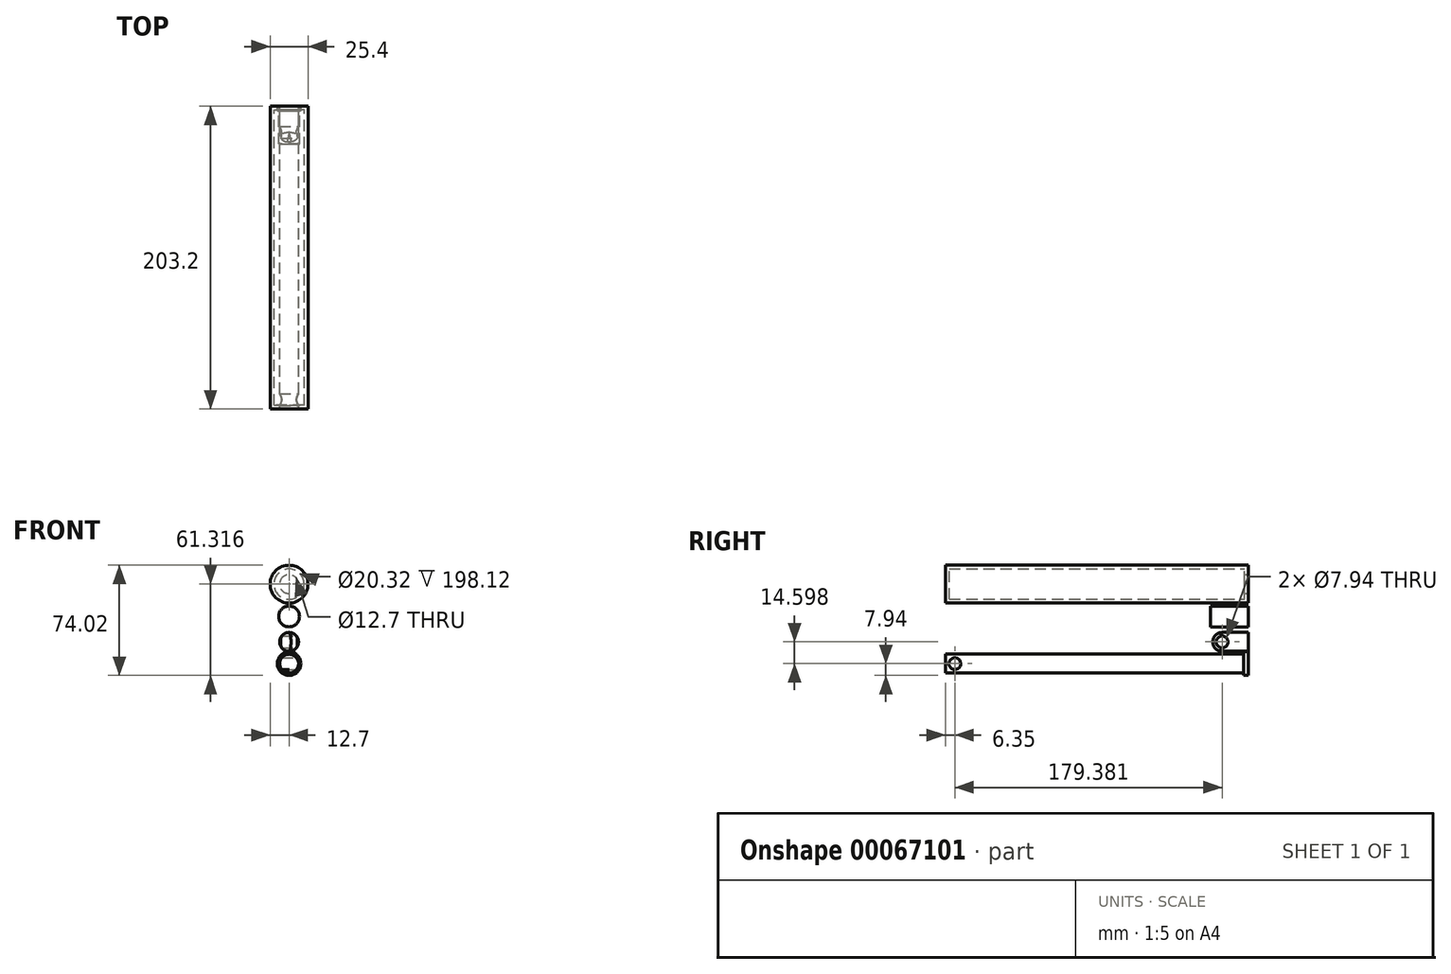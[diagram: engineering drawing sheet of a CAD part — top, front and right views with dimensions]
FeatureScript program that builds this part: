
annotation { "Feature Type Name" : "Feature", "Feature Type Description" : "" }
export const myFeature = defineFeature(function(context is Context, id is Id, definition is map)
    precondition{}
    {
        {
            var Q0;
            Q0=qCreatedBy(makeId("Front.planeOp"),FACE);
            var sketch = newSketch(context, id + "F0", { "sketchPlane" : qUnion([Q0])});
            skCircle(sketch, "E0", {"center": v(0, 0) * mm, "radius": 6.35 * mm});
            skCircle(sketch, "E1", {"center": v(0, 53.38) * mm, "radius": 12.7 * mm});
            skCircle(sketch, "E2", {"center": v(0, 31.7) * mm, "radius": 6.99 * mm});
            skCircle(sketch, "E3", {"center": v(0, 14.6) * mm, "radius": 6.35 * mm});
            skSolve(sketch);
        }
        {
            var Q0;
            Q0=makeQuery(id+"F0.imprint","IMPRINT",FACE,{"disambiguationData":[TD([[makeQuery(id+"F0.imprint","IMPRINT",EDGE,{"derivedFrom":sQuery(id+"F0.wireOp",EDGE,"E1")}),1.0]])]});
            var Q1;
            Q1=makeQuery(id+"F0.imprint","IMPRINT",FACE,{"disambiguationData":[TD([[makeQuery(id+"F0.imprint","IMPRINT",EDGE,{"derivedFrom":sQuery(id+"F0.wireOp",EDGE,"E0")}),1.0]])]});
            extrude(context, id + "F1", {"entities" : qUnion([Q0, Q1]), "depth" : 203.2 * mm});
        }
        {
            var Q0;
            Q0=makeQuery(id+"F0.imprint","IMPRINT",FACE,{"disambiguationData":[TD([[makeQuery(id+"F0.imprint","IMPRINT",EDGE,{"derivedFrom":sQuery(id+"F0.wireOp",EDGE,"E2")}),1.0]])]});
            var Q1;
            Q1=makeQuery(id+"F0.imprint","IMPRINT",FACE,{"disambiguationData":[TD([[makeQuery(id+"F0.imprint","IMPRINT",EDGE,{"derivedFrom":sQuery(id+"F0.wireOp",EDGE,"E3")}),1.0]])]});
            extrude(context, id + "F2", {"entities" : qUnion([Q0, Q1]), "depth" : 25.4 * mm});
        }
        {
            var Q0;
            Q0=makeQuery(id+"F1.opExtrude","CAP_FACE",FACE,{"disambiguationData":[OSD([sQuery(id+"F0.wireOp",EDGE,"E1")])],"isStart":false});
            var Q1;
            Q1=makeQuery(id+"F1.opExtrude","SWEPT_BODY",BODY,{"disambiguationData":[OSD([sQuery(id+"F0.wireOp",EDGE,"E1")])]});
            shell(context, id + "F3", {"isHollow" : true, "entities" : qUnion([Q0]), "parts" : qUnion([Q1]), "thickness" : 2.54 * mm});
        }
        {
            var Q0;
            Q0=makeQuery(id+"F0.imprint","IMPRINT",FACE,{"disambiguationData":[TD([[makeQuery(id+"F0.imprint","IMPRINT",EDGE,{"derivedFrom":sQuery(id+"F0.wireOp",EDGE,"E0")}),1.0]])]});
            var sketch = newSketch(context, id + "F4", { "sketchPlane" : qUnion([Q0])});
            skCircle(sketch, "E4.0", {"center": v(0, 0) * mm, "radius": 6.35 * mm});
            skCircle(sketch, "E4.1", {"center": v(0, 53.38) * mm, "radius": 12.7 * mm});
            skCircle(sketch, "E5", {"center": v(0, 53.38) * mm, "radius": 6.35 * mm});
            skCircle(sketch, "E6", {"center": v(0, 0) * mm, "radius": 7.94 * mm});
            skSolve(sketch);
        }
        {
            var Q0;
            Q0=makeQuery(id+"F4.imprint","IMPRINT",FACE,{"disambiguationData":[TD([[makeQuery(id+"F4.imprint","IMPRINT",EDGE,{"derivedFrom":sQuery(id+"F4.wireOp",EDGE,"E5")}),1.0]])]});
            extrude(context, id + "F5", {"entities" : qUnion([Q0]), "operationType" : NewBodyOperationType.REMOVE, "depth" : 200.66 * mm});
        }
        {
            var Q0;
            Q0=makeQuery(id+"F4.imprint","IMPRINT",FACE,{"disambiguationData":[TD([[makeQuery(id+"F4.imprint","IMPRINT",EDGE,{"derivedFrom":sQuery(id+"F4.wireOp",EDGE,"E4.0")}),-1.0]])]});
            extrude(context, id + "F6", {"entities" : qUnion([Q0]), "operationType" : NewBodyOperationType.ADD, "depth" : 3.17 * mm});
        }
        {
            var Q0;
            Q0=qCreatedBy(makeId("Right.planeOp"),FACE);
            var sketch = newSketch(context, id + "F7", { "sketchPlane" : qUnion([Q0])});
            skLineSegment(sketch, "E7.0", {"start": v(-203.2, -6.35) * mm, "end": v(-203.2, 6.35) * mm});
            skLineSegment(sketch, "E8", {"start": v(-203.2, 6.35) * mm, "end": v(-196.85, 0) * mm});
            skLineSegment(sketch, "E9", {"start": v(-196.85, 0) * mm, "end": v(-203.2, -6.35) * mm});
            skCircle(sketch, "E10", {"center": v(-196.85, 0) * mm, "radius": 3.97 * mm});
            skSolve(sketch);
        }
        {
            var Q0;
            Q0=qCreatedBy(makeId("Right.planeOp"),FACE);
            cPlane(context, id + "F8", {"entities" : qUnion([Q0]), "cplaneType" : CPlaneType.OFFSET, "offset" : 50.8 * mm, "width" : 152.4 * mm, "height" : 152.4 * mm});
        }
        {
            var Q0;
            Q0=qCreatedBy(id+"F8.planeOp",FACE);
            var sketch = newSketch(context, id + "F9", { "sketchPlane" : qUnion([Q0])});
            skCircle(sketch, "E11.0", {"center": v(-196.85, 0) * mm, "radius": 3.97 * mm});
            skSolve(sketch);
        }
        {
            var Q0;
            Q0=makeQuery(id+"F9.imprint","IMPRINT",FACE,{"disambiguationData":[TD([[makeQuery(id+"F9.imprint","IMPRINT",EDGE,{"derivedFrom":sQuery(id+"F9.wireOp",EDGE,"E11.0")}),1.0]])]});
            extrude(context, id + "F10", {"entities" : qUnion([Q0]), "operationType" : NewBodyOperationType.REMOVE, "endBound" : BoundingType.THROUGH_ALL, "oppositeDirection" : true, "depth" : 25.4 * mm});
        }
        {
            var Q0;
            Q0=qCreatedBy(id+"F8.planeOp",FACE);
            var sketch = newSketch(context, id + "F11", { "sketchPlane" : qUnion([Q0])});
            skLineSegment(sketch, "E12.0", {"start": v(-25.4, 8.25) * mm, "end": v(-25.4, 20.95) * mm});
            skLineSegment(sketch, "E13", {"start": v(-25.4, 20.95) * mm, "end": v(-17.47, 14.6) * mm, "construction": true});
            skLineSegment(sketch, "E14", {"start": v(-17.47, 14.6) * mm, "end": v(-25.4, 8.25) * mm, "construction": true});
            skLineSegment(sketch, "E15", {"start": v(-25.4, 14.6) * mm, "end": v(-7.03, 14.6) * mm, "construction": true});
            skCircle(sketch, "E16", {"center": v(-17.47, 14.6) * mm, "radius": 3.97 * mm});
            skCircle(sketch, "E17", {"center": v(-17.47, 14.6) * mm, "radius": 6.35 * mm});
            skLineSegment(sketch, "E18.0", {"start": v(0, 8.25) * mm, "end": v(0, 20.95) * mm});
            skLineSegment(sketch, "E19", {"start": v(-25.4, 20.95) * mm, "end": v(0, 20.95) * mm});
            skLineSegment(sketch, "E20", {"start": v(0, 8.25) * mm, "end": v(-25.4, 8.25) * mm});
            skSolve(sketch);
        }
        {
            var Q0;
            Q0=makeQuery(id+"F11.imprint","IMPRINT",FACE,{"disambiguationData":[TD([[makeQuery(id+"F11.imprint","IMPRINT",EDGE,{"derivedFrom":sQuery(id+"F11.wireOp",EDGE,"E16")}),1.0]])]});
            var Q1;
            {var subQ0=sQuery(id+"F11.wireOp",EDGE,"E12.0");Q1=makeQuery(id+"F11.imprint","IMPRINT",FACE,{"disambiguationData":[TD([[makeQuery(id+"F11.imprint","IMPRINT",EDGE,{"derivedFrom":subQ0}),-1.0]])]});}
            extrude(context, id + "F12", {"entities" : qUnion([Q0, Q1]), "operationType" : NewBodyOperationType.REMOVE, "endBound" : BoundingType.THROUGH_ALL, "oppositeDirection" : true, "depth" : 25.4 * mm});
        }
        {
            var Q0;
            Q0=makeQuery(id+"F12.boolean.opBoolean","INTERSECT",EDGE,{"disambiguationData":[OD(1.0)],"derivedFrom":[makeQuery(id+"F2.opExtrude","SWEPT_FACE",FACE,{"disambiguationData":[OSD([sQuery(id+"F0.wireOp",EDGE,"E3")])]}),makeQuery(id+"F12.opExtrude","SWEPT_FACE",FACE,{"disambiguationData":[OSD([sQuery(id+"F11.wireOp",EDGE,"E17")])]})]});
            var Q1;
            Q1=makeQuery(id+"F12.boolean.opBoolean","INTERSECT",EDGE,{"disambiguationData":[OD(0.0)],"derivedFrom":[makeQuery(id+"F2.opExtrude","SWEPT_FACE",FACE,{"disambiguationData":[OSD([sQuery(id+"F0.wireOp",EDGE,"E3")])]}),makeQuery(id+"F12.opExtrude","SWEPT_FACE",FACE,{"disambiguationData":[OSD([sQuery(id+"F11.wireOp",EDGE,"E17")])]})]});
            fillet(context, id + "F13", {"entities" : qUnion([Q0, Q1]), "radius" : 5.08 * mm, "tangentPropagation" : true, "allowEdgeOverflow" : false});
        }
    });
